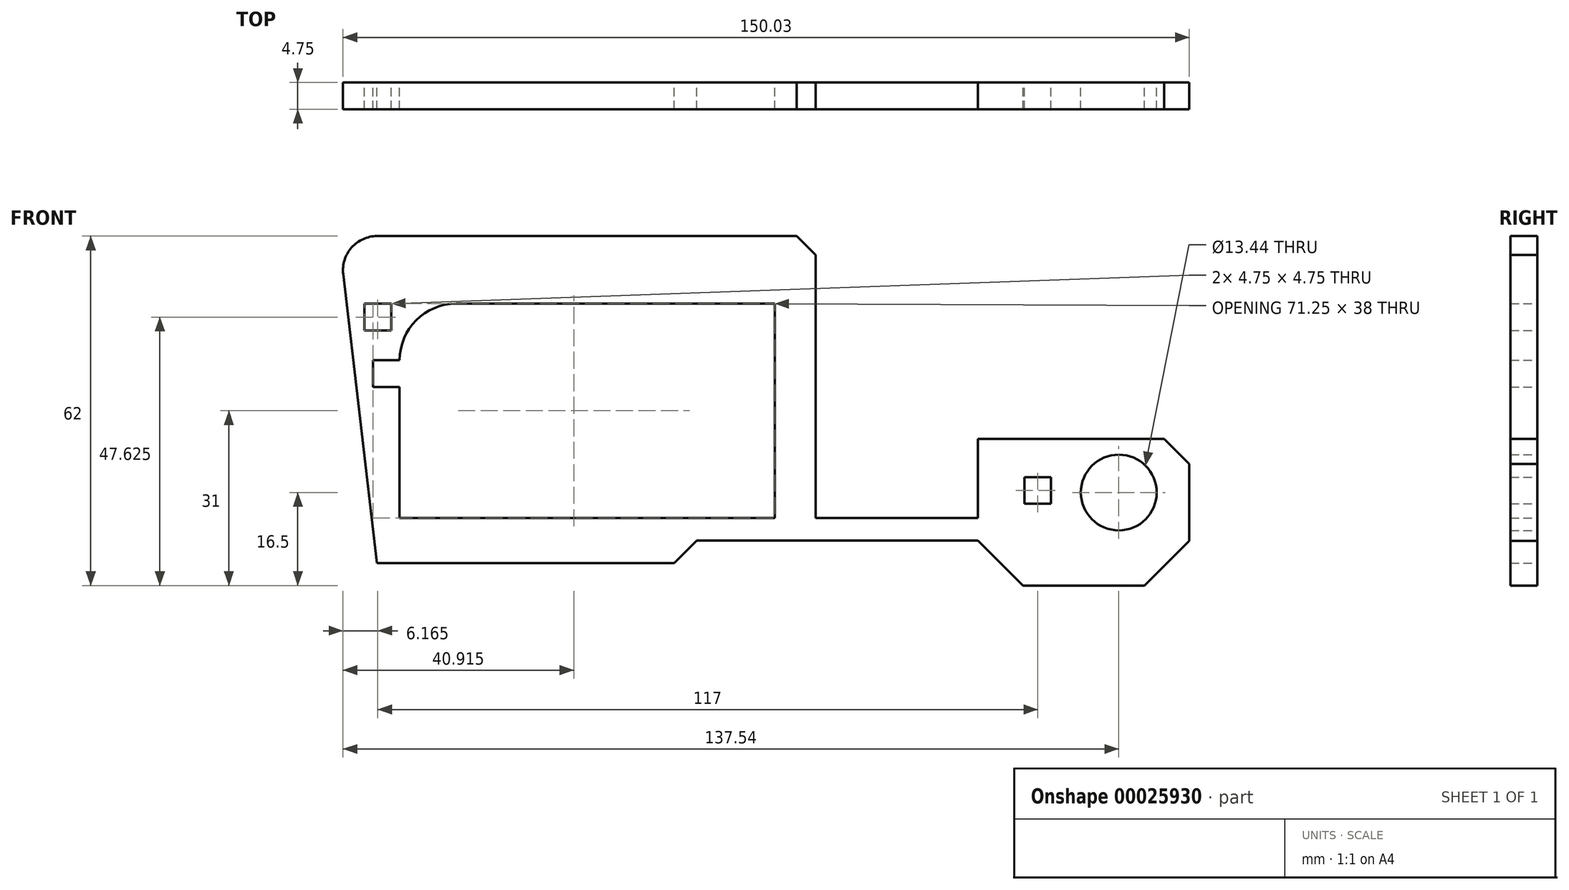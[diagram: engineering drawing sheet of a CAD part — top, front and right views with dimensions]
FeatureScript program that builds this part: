
annotation { "Feature Type Name" : "Feature", "Feature Type Description" : "" }
export const myFeature = defineFeature(function(context is Context, id is Id, definition is map)
    precondition{}
    {
        {
            var Q0;
            Q0=qCreatedBy(makeId("Front.planeOp"),FACE);
            var sketch = newSketch(context, id + "F0", { "sketchPlane" : qUnion([Q0])});
            skLineSegment(sketch, "E0.bottom", {"start": v(0, 0) * mm, "end": v(66.5, 0) * mm});
            skLineSegment(sketch, "E0.top", {"start": v(10, 38) * mm, "end": v(66.5, 38) * mm});
            skLineSegment(sketch, "E0.left", {"start": v(0, 0) * mm, "end": v(0, 23.25) * mm});
            skLineSegment(sketch, "E0.right", {"start": v(66.5, 0) * mm, "end": v(66.5, 38) * mm});
            skLineSegment(sketch, "E1", {"start": v(-4, -8) * mm, "end": v(48.64, -8) * mm});
            skLineSegment(sketch, "E2", {"start": v(48.64, -8) * mm, "end": v(52.64, -4) * mm});
            skLineSegment(sketch, "E3", {"start": v(52.64, -4) * mm, "end": v(102.5, -4) * mm});
            skLineSegment(sketch, "E4", {"start": v(102.5, -4) * mm, "end": v(110.5, -12) * mm});
            skLineSegment(sketch, "E5", {"start": v(110.5, -12) * mm, "end": v(132.04, -12) * mm});
            skLineSegment(sketch, "E6", {"start": v(70.39, 50) * mm, "end": v(-4, 50) * mm});
            skArc(sketch, "E7", {"start": v(-4, 50) * mm, "mid": v(-8.51, 47.97) * mm, "end": v(-10, 43.26) * mm});
            skLineSegment(sketch, "E8", {"start": v(-10, 43.26) * mm, "end": v(-4, -8) * mm});
            skCircle(sketch, "E9", {"center": v(127.5, 4.5) * mm, "radius": 6.72 * mm});
            skLineSegment(sketch, "E10", {"start": v(70.39, 50) * mm, "end": v(73.77, 46.62) * mm});
            skLineSegment(sketch, "E11", {"start": v(73.77, 46.62) * mm, "end": v(73.77, 0) * mm});
            skLineSegment(sketch, "E12", {"start": v(73.77, 0) * mm, "end": v(102.5, 0) * mm});
            skLineSegment(sketch, "E13", {"start": v(102.5, 0) * mm, "end": v(102.5, 14.04) * mm});
            skLineSegment(sketch, "E14", {"start": v(102.5, 14.04) * mm, "end": v(135.53, 14.04) * mm});
            skLineSegment(sketch, "E15", {"start": v(135.53, 14.04) * mm, "end": v(139.99, 9.58) * mm});
            skLineSegment(sketch, "E16", {"start": v(139.99, 9.58) * mm, "end": v(139.99, -4.06) * mm});
            skLineSegment(sketch, "E17", {"start": v(139.99, -4.06) * mm, "end": v(132.04, -12) * mm});
            skLineSegment(sketch, "E18.bottom", {"start": v(-1.5, 38) * mm, "end": v(-6.25, 38) * mm});
            skLineSegment(sketch, "E18.top", {"start": v(-1.5, 33.25) * mm, "end": v(-6.25, 33.25) * mm});
            skLineSegment(sketch, "E18.left", {"start": v(-1.5, 38) * mm, "end": v(-1.5, 33.25) * mm});
            skLineSegment(sketch, "E18.right", {"start": v(-6.25, 38) * mm, "end": v(-6.25, 33.25) * mm});
            skLineSegment(sketch, "E19.bottom", {"start": v(110.75, 7.25) * mm, "end": v(115.5, 7.25) * mm});
            skLineSegment(sketch, "E19.top", {"start": v(110.75, 2.5) * mm, "end": v(115.5, 2.5) * mm});
            skLineSegment(sketch, "E19.left", {"start": v(110.75, 7.25) * mm, "end": v(110.75, 2.5) * mm});
            skLineSegment(sketch, "E19.right", {"start": v(115.5, 7.25) * mm, "end": v(115.5, 2.5) * mm});
            skLineSegment(sketch, "E20", {"start": v(0, 28) * mm, "end": v(-4.75, 28) * mm});
            skLineSegment(sketch, "E21", {"start": v(-4.75, 28) * mm, "end": v(-4.75, 23.25) * mm});
            skLineSegment(sketch, "E22", {"start": v(-4.75, 23.25) * mm, "end": v(0, 23.25) * mm});
            skLineSegment(sketch, "E23.trimOffspring", {"start": v(0, 28) * mm, "end": v(0, 28) * mm});
            skPoint(sketch, "E24.visualSharp", {"position": v(0, 38) * mm});
            skArc(sketch, "E24.filletArc", {"start": v(10, 38) * mm, "mid": v(2.93, 35.07) * mm, "end": v(0, 28) * mm});
            skSolve(sketch);
        }
        {
            var Q0;
            Q0=qSketchRegion(id+"F0",true);
            extrude(context, id + "F1", {"entities" : qUnion([Q0]), "depth" : 4.75 * mm});
        }
    });
